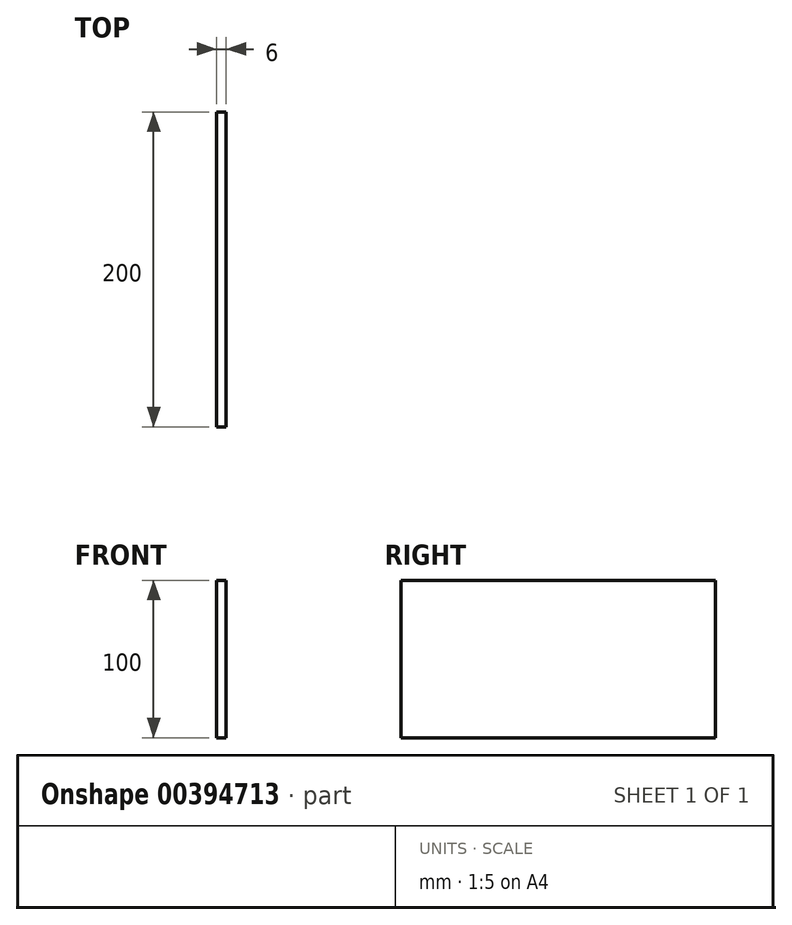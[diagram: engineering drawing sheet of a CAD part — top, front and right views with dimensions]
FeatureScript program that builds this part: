
annotation { "Feature Type Name" : "Feature", "Feature Type Description" : "" }
export const myFeature = defineFeature(function(context is Context, id is Id, definition is map)
    precondition{}
    {
        {
            var Q0;
            Q0=qCreatedBy(makeId("Right.planeOp"),FACE);
            var sketch = newSketch(context, id + "F0", { "sketchPlane" : qUnion([Q0])});
            skLineSegment(sketch, "E0.bottom", {"start": v(0, 0) * mm, "end": v(200, 0) * mm});
            skLineSegment(sketch, "E0.top", {"start": v(0, 100) * mm, "end": v(200, 100) * mm});
            skLineSegment(sketch, "E0.left", {"start": v(0, 0) * mm, "end": v(0, 100) * mm});
            skLineSegment(sketch, "E0.right", {"start": v(200, 0) * mm, "end": v(200, 100) * mm});
            skSolve(sketch);
        }
        {
            var Q0;
            Q0 = qSketchRegion(id + "F0", true);
            extrude(context, id + "F1", {"entities" : qUnion([Q0]), "depth" : 6 * mm});
        }
    });
